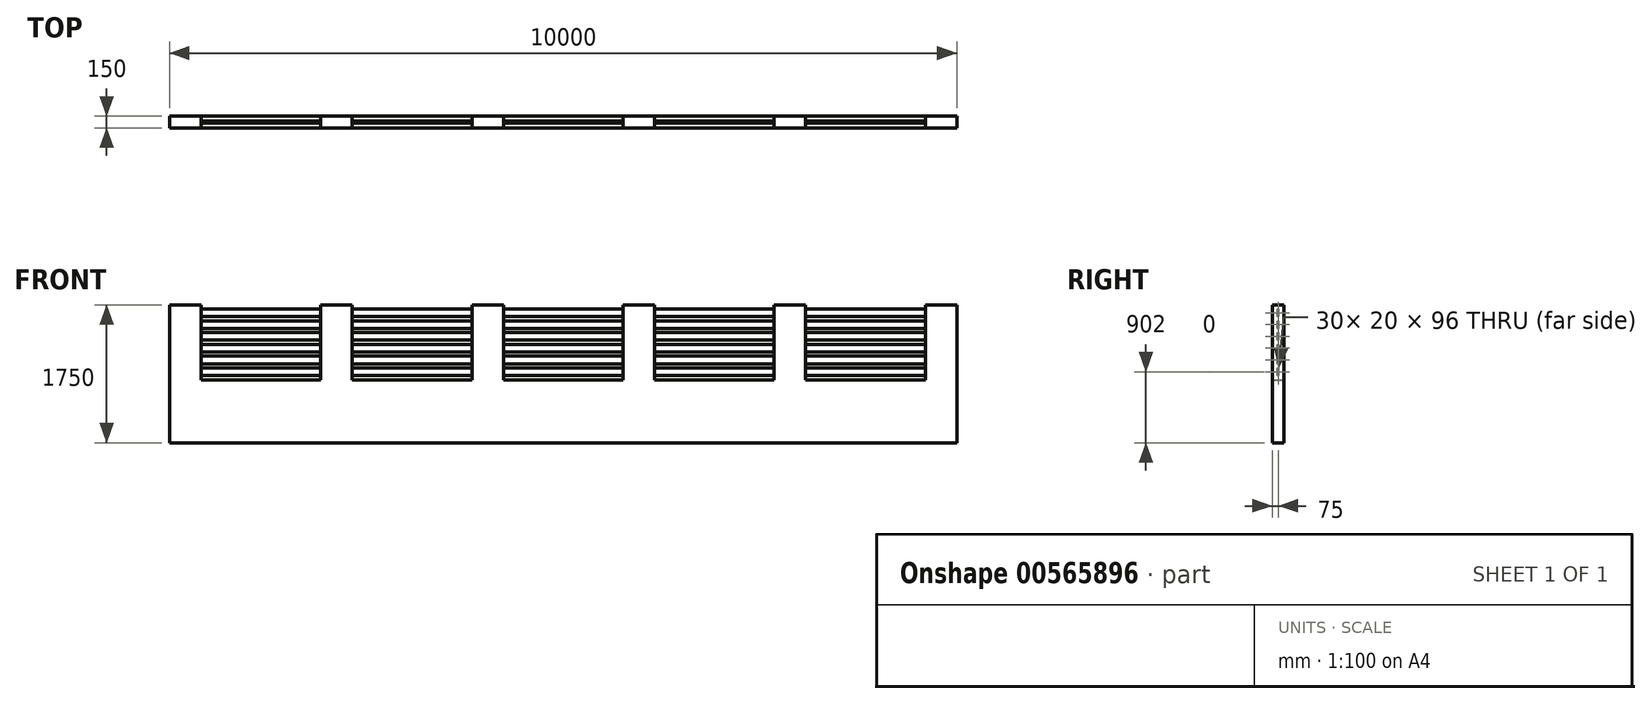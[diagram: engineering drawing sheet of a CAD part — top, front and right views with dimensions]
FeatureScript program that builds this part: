
annotation { "Feature Type Name" : "Feature", "Feature Type Description" : "" }
export const myFeature = defineFeature(function(context is Context, id is Id, definition is map)
    precondition{}
    {
        {
            var Q0;
            Q0=qCreatedBy(makeId("Top.planeOp"),FACE);
            cPlane(context, id + "F0", {"entities" : qUnion([Q0]), "cplaneType" : CPlaneType.OFFSET, "offset" : 800 * mm, "width" : 150 * mm, "height" : 150 * mm});
        }
        {
            var Q0;
            Q0=qCreatedBy(makeId("Top.planeOp"),FACE);
            cPlane(context, id + "F1", {"entities" : qUnion([Q0]), "cplaneType" : CPlaneType.OFFSET, "offset" : 1750 * mm, "width" : 150 * mm, "height" : 150 * mm});
        }
        {
            var Q0;
            Q0=qCreatedBy(makeId("Top.planeOp"),FACE);
            var sketch = newSketch(context, id + "F2", { "sketchPlane" : qUnion([Q0])});
            skLineSegment(sketch, "E0.bottom", {"start": v(0, 0) * mm, "end": v(10000, 0) * mm});
            skLineSegment(sketch, "E0.top", {"start": v(0, 150) * mm, "end": v(10000, 150) * mm});
            skLineSegment(sketch, "E0.left", {"start": v(0, 0) * mm, "end": v(0, 150) * mm});
            skLineSegment(sketch, "E0.right", {"start": v(10000, 0) * mm, "end": v(10000, 150) * mm});
            skSolve(sketch);
        }
        {
            var Q0;
            Q0=makeQuery(id+"F2.imprint","IMPRINT",FACE,{"disambiguationData":[TD([[makeQuery(id+"F2.imprint","IMPRINT",EDGE,{"derivedFrom":sQuery(id+"F2.wireOp",EDGE,"E0.bottom")}),1.0]])]});
            var Q1;
            Q1=qCreatedBy(id+"F0.planeOp",FACE);
            extrude(context, id + "F3", {"entities" : qUnion([Q0]), "endBound" : BoundingType.UP_TO_SURFACE, "depth" : 25 * mm, "endBoundEntityFace" : qUnion([Q1]), "offsetDistance" : 25 * mm});
        }
        {
            var Q0;
            Q0=qCreatedBy(makeId("Top.planeOp"),FACE);
            var sketch = newSketch(context, id + "F4", { "sketchPlane" : qUnion([Q0])});
            skPoint(sketch, "E1.0", {"position": v(0, 150) * mm});
            skLineSegment(sketch, "E2.bottom", {"start": v(0, 150) * mm, "end": v(400, 150) * mm});
            skLineSegment(sketch, "E2.top", {"start": v(0, 0) * mm, "end": v(400, 0) * mm});
            skLineSegment(sketch, "E2.left", {"start": v(0, 150) * mm, "end": v(0, 0) * mm});
            skLineSegment(sketch, "E2.right", {"start": v(400, 150) * mm, "end": v(400, 0) * mm});
            skLineSegment(sketch, "E3.1.0.0", {"start": v(1920, 150) * mm, "end": v(2320, 150) * mm});
            skLineSegment(sketch, "E3.1.0.1", {"start": v(1920, 150) * mm, "end": v(1920, 0) * mm});
            skLineSegment(sketch, "E3.1.0.2", {"start": v(1920, 0) * mm, "end": v(2320, 0) * mm});
            skLineSegment(sketch, "E3.1.0.3", {"start": v(2320, 150) * mm, "end": v(2320, 0) * mm});
            skLineSegment(sketch, "E3.2.0.0", {"start": v(3840, 150) * mm, "end": v(4240, 150) * mm});
            skLineSegment(sketch, "E3.2.0.1", {"start": v(3840, 150) * mm, "end": v(3840, 0) * mm});
            skLineSegment(sketch, "E3.2.0.2", {"start": v(3840, 0) * mm, "end": v(4240, 0) * mm});
            skLineSegment(sketch, "E3.2.0.3", {"start": v(4240, 150) * mm, "end": v(4240, 0) * mm});
            skLineSegment(sketch, "E3.3.0.0", {"start": v(5760, 150) * mm, "end": v(6160, 150) * mm});
            skLineSegment(sketch, "E3.3.0.1", {"start": v(5760, 150) * mm, "end": v(5760, 0) * mm});
            skLineSegment(sketch, "E3.3.0.2", {"start": v(5760, 0) * mm, "end": v(6160, 0) * mm});
            skLineSegment(sketch, "E3.3.0.3", {"start": v(6160, 150) * mm, "end": v(6160, 0) * mm});
            skLineSegment(sketch, "E3.4.0.0", {"start": v(7680, 150) * mm, "end": v(8080, 150) * mm});
            skLineSegment(sketch, "E3.4.0.1", {"start": v(7680, 150) * mm, "end": v(7680, 0) * mm});
            skLineSegment(sketch, "E3.4.0.2", {"start": v(7680, 0) * mm, "end": v(8080, 0) * mm});
            skLineSegment(sketch, "E3.4.0.3", {"start": v(8080, 150) * mm, "end": v(8080, 0) * mm});
            skLineSegment(sketch, "E3.5.0.0", {"start": v(9600, 150) * mm, "end": v(10000, 150) * mm});
            skLineSegment(sketch, "E3.5.0.1", {"start": v(9600, 150) * mm, "end": v(9600, 0) * mm});
            skLineSegment(sketch, "E3.5.0.2", {"start": v(9600, 0) * mm, "end": v(10000, 0) * mm});
            skLineSegment(sketch, "E3.5.0.3", {"start": v(10000, 150) * mm, "end": v(10000, 0) * mm});
            skLineSegment(sketch, "E3.direction1", {"start": v(0, 0) * mm, "end": v(1920, 0) * mm, "construction": true});
            skSolve(sketch);
        }
        {
            var Q0;
            Q0 = qSketchRegion(id + "F4", true);
            var Q1;
            Q1=qCreatedBy(id+"F1.planeOp",FACE);
            var Q2;
            Q2=qCreatedBy(id+"F1.planeOp",FACE);
            extrude(context, id + "F5", {"entities" : qUnion([Q0]), "operationType" : NewBodyOperationType.ADD, "endBound" : BoundingType.UP_TO_SURFACE, "depth" : 25 * mm, "endBoundEntityFace" : qUnion([Q1]), "offsetDistance" : 25 * mm});
        }
        {
            var Q0;
            Q0=qCreatedBy(makeId("Right.planeOp"),FACE);
            var sketch = newSketch(context, id + "F6", { "sketchPlane" : qUnion([Q0])});
            skLineSegment(sketch, "E4.0", {"start": v(0, 0) * mm, "end": v(150, 0) * mm});
            skLineSegment(sketch, "E5.0", {"start": v(150, 1750) * mm, "end": v(0, 1750) * mm});
            skLineSegment(sketch, "E6", {"start": v(75, 1750) * mm, "end": v(75, 0) * mm, "construction": true});
            skLineSegment(sketch, "E7", {"start": v(85, 1750) * mm, "end": v(85, 0) * mm, "construction": true});
            skLineSegment(sketch, "E8.bottom", {"start": v(85, 1700) * mm, "end": v(65, 1700) * mm});
            skLineSegment(sketch, "E8.top", {"start": v(85, 1604) * mm, "end": v(65, 1604) * mm});
            skLineSegment(sketch, "E8.left", {"start": v(85, 1700) * mm, "end": v(85, 1604) * mm});
            skLineSegment(sketch, "E8.right", {"start": v(65, 1700) * mm, "end": v(65, 1604) * mm});
            skLineSegment(sketch, "E9.0.1.0", {"start": v(85, 1550) * mm, "end": v(85, 1454) * mm});
            skLineSegment(sketch, "E9.0.1.1", {"start": v(85, 1454) * mm, "end": v(65, 1454) * mm});
            skLineSegment(sketch, "E9.0.1.2", {"start": v(65, 1550) * mm, "end": v(65, 1454) * mm});
            skLineSegment(sketch, "E9.0.1.3", {"start": v(85, 1550) * mm, "end": v(65, 1550) * mm});
            skLineSegment(sketch, "E9.0.2.0", {"start": v(85, 1400) * mm, "end": v(85, 1304) * mm});
            skLineSegment(sketch, "E9.0.2.1", {"start": v(85, 1304) * mm, "end": v(65, 1304) * mm});
            skLineSegment(sketch, "E9.0.2.2", {"start": v(65, 1400) * mm, "end": v(65, 1304) * mm});
            skLineSegment(sketch, "E9.0.2.3", {"start": v(85, 1400) * mm, "end": v(65, 1400) * mm});
            skLineSegment(sketch, "E9.0.3.0", {"start": v(85, 1250) * mm, "end": v(85, 1154) * mm});
            skLineSegment(sketch, "E9.0.3.1", {"start": v(85, 1154) * mm, "end": v(65, 1154) * mm});
            skLineSegment(sketch, "E9.0.3.2", {"start": v(65, 1250) * mm, "end": v(65, 1154) * mm});
            skLineSegment(sketch, "E9.0.3.3", {"start": v(85, 1250) * mm, "end": v(65, 1250) * mm});
            skLineSegment(sketch, "E9.0.4.0", {"start": v(85, 1100) * mm, "end": v(85, 1004) * mm});
            skLineSegment(sketch, "E9.0.4.1", {"start": v(85, 1004) * mm, "end": v(65, 1004) * mm});
            skLineSegment(sketch, "E9.0.4.2", {"start": v(65, 1100) * mm, "end": v(65, 1004) * mm});
            skLineSegment(sketch, "E9.0.4.3", {"start": v(85, 1100) * mm, "end": v(65, 1100) * mm});
            skLineSegment(sketch, "E9.0.5.0", {"start": v(85, 950) * mm, "end": v(85, 854) * mm});
            skLineSegment(sketch, "E9.0.5.1", {"start": v(85, 854) * mm, "end": v(65, 854) * mm});
            skLineSegment(sketch, "E9.0.5.2", {"start": v(65, 950) * mm, "end": v(65, 854) * mm});
            skLineSegment(sketch, "E9.0.5.3", {"start": v(85, 950) * mm, "end": v(65, 950) * mm});
            skLineSegment(sketch, "E9.direction1", {"start": v(65, 1604) * mm, "end": v(90, 1604) * mm, "construction": true});
            skLineSegment(sketch, "E9.direction2", {"start": v(65, 1604) * mm, "end": v(65, 1454) * mm, "construction": true});
            skSolve(sketch);
        }
        {
            var Q0;
            Q0 = qSketchRegion(id + "F6", true);
            var Q1;
            Q1=makeQuery(id+"F5.boolean.opBoolean","MERGE",FACE,{"derivedFrom":[makeQuery(id+"F3.opExtrude","SWEPT_FACE",FACE,{"disambiguationData":[OSD([sQuery(id+"F2.wireOp",EDGE,"E0.right")])]}),makeQuery(id+"F5.opExtrude","SWEPT_FACE",FACE,{"disambiguationData":[OSD([sQuery(id+"F4.wireOp",EDGE,"E3.10.0.3")])]})]});
            var Q2;
            Q2=makeQuery(id+"F3.opExtrude","SWEPT_BODY",BODY,{"disambiguationData":[OSD([sQuery(id+"F2.wireOp",EDGE,"E0.bottom"),sQuery(id+"F2.wireOp",EDGE,"E0.top"),sQuery(id+"F2.wireOp",EDGE,"E0.left"),sQuery(id+"F2.wireOp",EDGE,"E0.right")])]});
            extrude(context, id + "F7", {"entities" : qUnion([Q0]), "operationType" : NewBodyOperationType.ADD, "endBound" : BoundingType.UP_TO_SURFACE, "depth" : 25 * mm, "endBoundEntityFace" : qUnion([Q1]), "endBoundEntityBody" : qUnion([Q2]), "offsetDistance" : 25 * mm});
        }
    });
